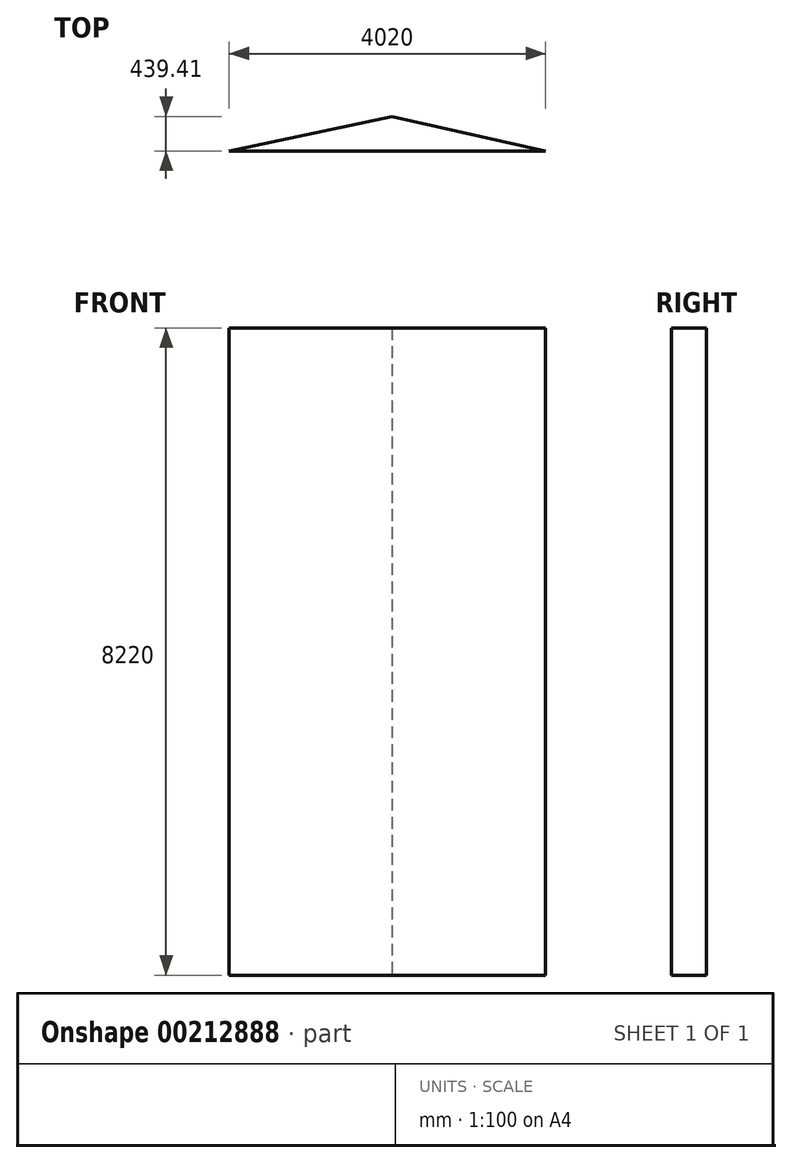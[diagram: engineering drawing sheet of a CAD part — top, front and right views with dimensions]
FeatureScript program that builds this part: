
annotation { "Feature Type Name" : "Feature", "Feature Type Description" : "" }
export const myFeature = defineFeature(function(context is Context, id is Id, definition is map)
    precondition{}
    {
        {
            var Q0;
            Q0=qCreatedBy(makeId("Top.planeOp"),FACE);
            var sketch = newSketch(context, id + "F0", { "sketchPlane" : qUnion([Q0])});
            skLineSegment(sketch, "E0.top", {"start": v(-2067.26, -2261.09) * mm, "end": v(1952.74, -2261.09) * mm});
            skPoint(sketch, "E0.middle", {"position": v(0, 0) * mm});
            skLineSegment(sketch, "E1", {"start": v(-2067.26, -2261.09) * mm, "end": v(0, -1821.68) * mm});
            skLineSegment(sketch, "E2", {"start": v(0, -1821.68) * mm, "end": v(1952.74, -2261.09) * mm});
            skPoint(sketch, "E0.left.start.orphan", {"position": v(-1952.74, 2261.09) * mm});
            skPoint(sketch, "E0.right.start.orphan", {"position": v(2067.26, 2261.09) * mm});
            skSolve(sketch);
        }
        {
            var Q0;
            Q0=qSketchRegion(id+"F0",true);
            extrude(context, id + "F1", {"entities" : qUnion([Q0]), "depth" : (8500 - 200 - 80) * mm});
        }
    });
